# Revit family: cl_31_bulkhead_5cl761603
name_source: partatom
category: Lighting Fixtures
units: mm (PartAtom-declared; Revit-internal decimal feet)

## family parameters
Cut with Voids When Loaded = No
Host = Face
Light Source = No
Part Type = Normal
Room Calculation Point = No
Round Connector Dimension = Use Diameter
Shared = No

## types (1)
- --- (1 x LED, 1570 lm, 14.9 W, 3000K)
    Apparent Load = 15 VA
    CIE Flux Codes = 46 78 95 100 100
    Color Rendering = 80
    Color Temperature = 3000K
    Default Elevation = 1800 mm
    Description = CL 31 Bulkhead, wall and ceiling luminaire, primary light control with reflector, primary optical cover: cover panel, of PC, opal, primary light characteristic: symmetric, installation type: surface-mounted, LED, rated luminous flux: 1.575lm, luminous efficacy: 105lm/W, light colour: 830, colour temperature: 3000K, control gear: DALI, with terminal, 5-pole, max. 2.5mm², mains connection: 220..240V, AC, 50/60Hz, rated input power: 15W, luminaire housing, square, of aluminium, powder-coated, SITECO metallic grey, length: 266mm, width: 266mm, height: 63mm, protection rating (complete): IP65, insulation class (complete): insulation class I (protective earthing), certification: CE, ENEC, impact resistance: IK09, permissible operating ambient temperature for outdoor applications: -20..+50°C, packaging unit: 1 piece
    Height = 63 mm
    Lamp = 1 x LED
    Lamp Light Flux = 1570 lm
    Lamp Power = 14.9 W
    Lamp count = 1
    Length = 266 mm
    Luminous efficacy = 105 lm/W
    Manufacturer = Siteco
    ModVariant = No
    Model = 5CL761603
    Mounting Place = Wall
    Mounting Type = Surface mounted
    Number of Poles = 1
    OnlyDefault = Yes
    Power Factor = 1
    Product Name = CL 31 Bulkhead
    Product group = wall and ceiling luminaire | wall mounted
    ProductGroupID = 2001
    Protection Class = Protection class I
    Protection Degree = IP 65
    RLX_Detail_Level = 1
    RLX_Emergency_Light_Flux = 0 lm
    RLX_Emergency_Type = 0
    RLX_Emergency_Type_DB = No
    RlxData = <blob elided: 47641 chars, md5=c971ff42>
    Socket = socket
    Standby Power = 0 W
    System Light Flux = 1570 lm
    System Power = 15 W
    Type Comments = factory setting: luminous flux: 100 % | dim-lin: 254 | 347 mA
    Type Image = l_1006889.jpg
    URL = http://relux.com
    VarID = @adj_194367
    Voltage = 0 V
    Weight = 0.00 kg
    Width = 266 mm

## geometry (parser evidence)
native form markers: Sweep x9
no freeform markers — native parametric forms only
